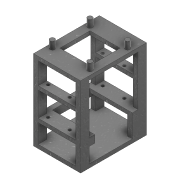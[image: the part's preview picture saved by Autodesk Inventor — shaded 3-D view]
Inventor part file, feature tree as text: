
AUTODESK INVENTOR PART (.ipt)
format: ipt  version: 2021 (Build 250183000, 183)  size: 300,032 bytes
history: native  units: mm
features: extrude x10, sketch x10, plane x1
ambient origin geometry x8: Origin, YZ Plane, XZ Plane, XY Plane, X Axis, Y Axis, Z Axis, Center Point
bodies: Solid1 (feature_tree)
feature tree (21):
  extrude  "Extrusion1"  Depth=70.0mm
  extrude  "Extrusion2"  Depth=5.0mm
  extrude  "Extrusion3"  Depth=70.0mm
  extrude  "Extrusion4"  Depth=40.0mm
  extrude  "Extrusion5"  Depth=4.0mm TaperAngle=0.0deg
  extrude  "Extrusion6"  Depth=58.0mm
  extrude  "Extrusion7"  Depth=6.0mm
  extrude  "Extrusion8"  Depth=3.0mm
  plane  "Work Plane1"
  extrude  "Extrusion9"  Depth=3.0mm
  extrude  "Extrusion10"  Depth=16.0mm
  sketch  "Sketch1"  dims[d0=50.0mm d1=70.0mm]
  sketch  "Sketch2"  dims[d2=4.0mm d3=0.0mm d4=5.0mm]
  sketch  "Sketch3"  dims[d5=5.0mm d6=70.0mm]
  sketch  "Sketch4"  dims[d7=20.0mm d8=0.0mm d9=40.0mm]
  sketch  "Sketch5"  dims[d10=40.0mm d11=4.0mm d12=0.0mm]
  sketch  "Sketch6"  dims[d13=23.0mm d14=58.0mm]
  sketch  "Sketch7"  dims[d15=6.0mm d16=4.5mm]
  sketch  "Sketch8"  dims[d17=3.0mm d18=3.0mm]
  sketch  "Sketch9"  dims[d19=3.0mm d20=3.0mm]
  sketch  "Sketch10"  dims[d21=52.0mm d22=16.0mm d23=8.0mm d24=9.0mm d25=5.0mm d26=0.0mm d27=9.0mm d28=9.0mm d29=53.0mm d30=0.0mm d31=20.0mm d32=20.0mm d33=50.0mm d34=50.0mm d35=40.0mm d36=40.0mm d37=32.0mm d38=32.0mm d39=4.0mm d40=0.0mm d41=40.0mm d42=40.0mm d43=5.0mm d44=5.0mm d45=5.0mm d46=5.0mm d47=8.0mm d48=0.0mm d51=5.0mm d52=0.0mm d53=40.0mm d54=30.0mm d55=4.0mm d56=0.0mm d57=5.0mm d58=0.0mm d49=0.5mm d50=0.872665mm]
